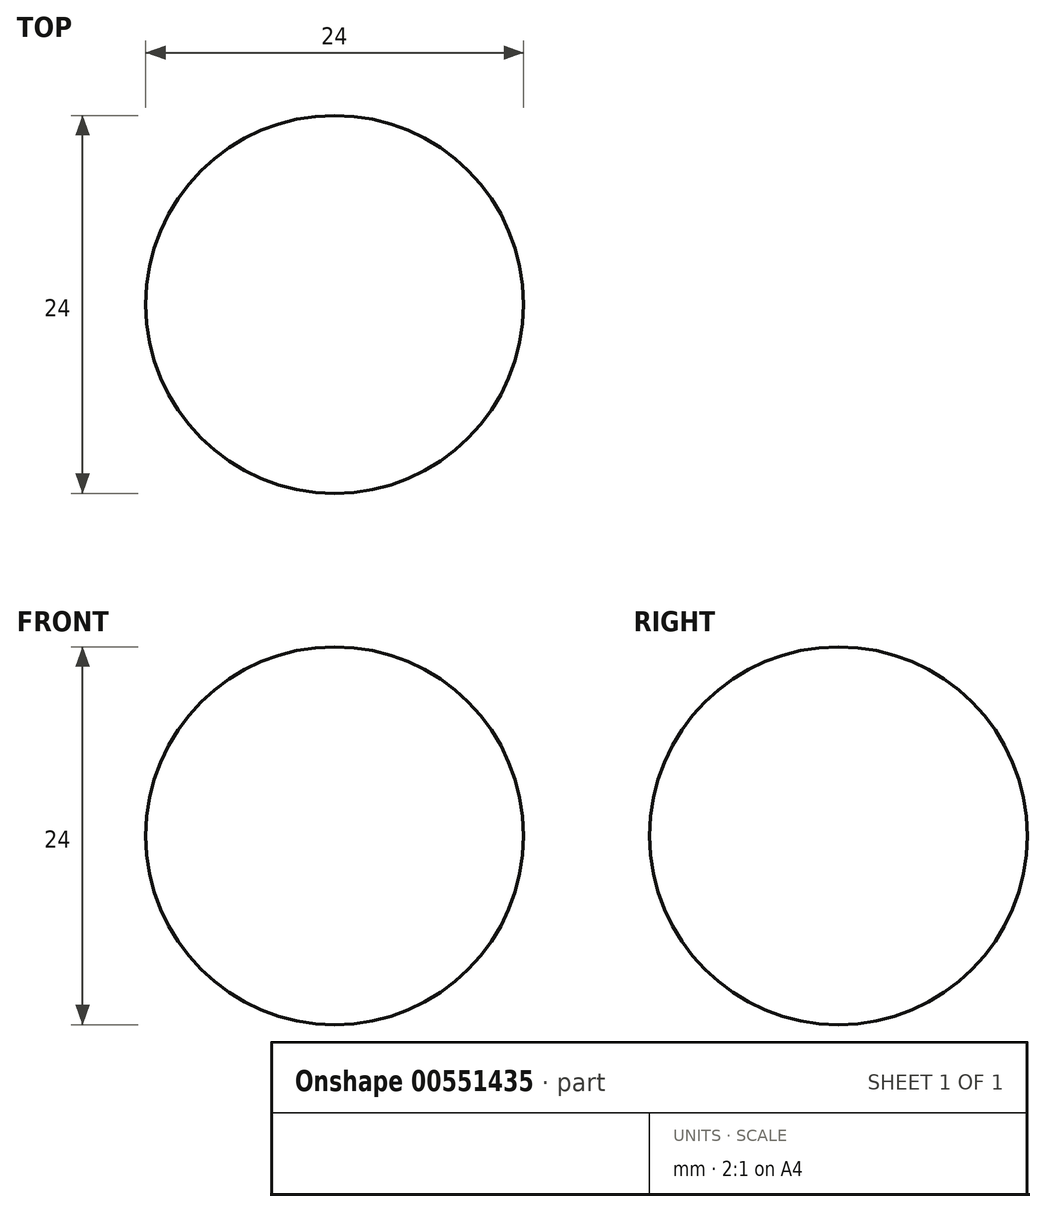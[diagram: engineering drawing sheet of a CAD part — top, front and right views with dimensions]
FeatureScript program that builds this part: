
annotation { "Feature Type Name" : "Feature", "Feature Type Description" : "" }
export const myFeature = defineFeature(function(context is Context, id is Id, definition is map)
    precondition{}
    {
        {
            var Q0;
            Q0=qCreatedBy(makeId("Top.planeOp"),FACE);
            var sketch = newSketch(context, id + "F0", { "sketchPlane" : qUnion([Q0])});
            skArc(sketch, "E0", {"start": v(0, -12) * mm, "mid": v(12, 0) * mm, "end": v(0, 12) * mm});
            skLineSegment(sketch, "E1", {"start": v(0, 16.68) * mm, "end": v(0, -26.89) * mm, "construction": true});
            skLineSegment(sketch, "E2", {"start": v(0, 12) * mm, "end": v(0, -12) * mm});
            skSolve(sketch);
        }
        {
            var Q0;
            Q0=qSketchRegion(id+"F0",true);
            var Q1;
            Q1=sQuery(id+"F0.wireOp",EDGE,"E1");
            revolve(context, id + "F1", {"entities" : qUnion([Q0]), "axis" : qUnion([Q1]), "revolveType" : RevolveType.FULL});
        }
    });
